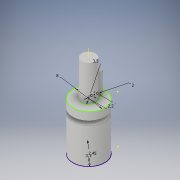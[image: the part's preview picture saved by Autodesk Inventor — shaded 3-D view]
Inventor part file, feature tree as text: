
AUTODESK INVENTOR PART (.ipt)
format: ipt  version: 2019 (Build 230136000, 136)  size: 138,240 bytes
history: native  units: in
note: dims shown in document units (in); Inventor stores cm internally (conversion verified against a paired STEP export)
features: extrude x5, sketch x2, other x1
ambient origin geometry x8: Origin, YZ Plane, XZ Plane, XY Plane, X Axis, Y Axis, Z Axis, Center Point
bodies: Solid1 (feature_tree)
feature tree (8):
  sketch  "Sketch1"  dims[d0=0.315in d1=0.0787in]
  extrude  "Extrusion1"  Depth=0.0787in
  extrude  "Extrusion2"  TaperAngle=0.0deg  [1 undecoded]
  extrude  "Extrusion3"  TaperAngle=0.0deg  [1 undecoded]
  sketch  "Sketch2"  dims[d3=0.1378in d4=0.0in d5=0.0in d6=0.0in d7=0.0787in d8=0.0in d9=0.2126in d10=0.0in d11=0.3543in d12=0.0in d13=0.4724in d14=0.0in d17=0.0866in d18=0.315in d19=0.122in d20=0.0965in d21=0.3543in d22=0.0in d23=0.2441in d24=0.0in]
  extrude  "Extrusion4"  TaperAngle=0.0deg  [1 undecoded]
  extrude  "Extrusion5"  Depth=0.0787in TaperAngle=0.0deg
  other  "Work Axis1"
note: 3 required parameter values undecoded (feature->parameter linkage not recoverable at this tier; creation-order binding heuristic only, values carry confidence <= 0.55)
